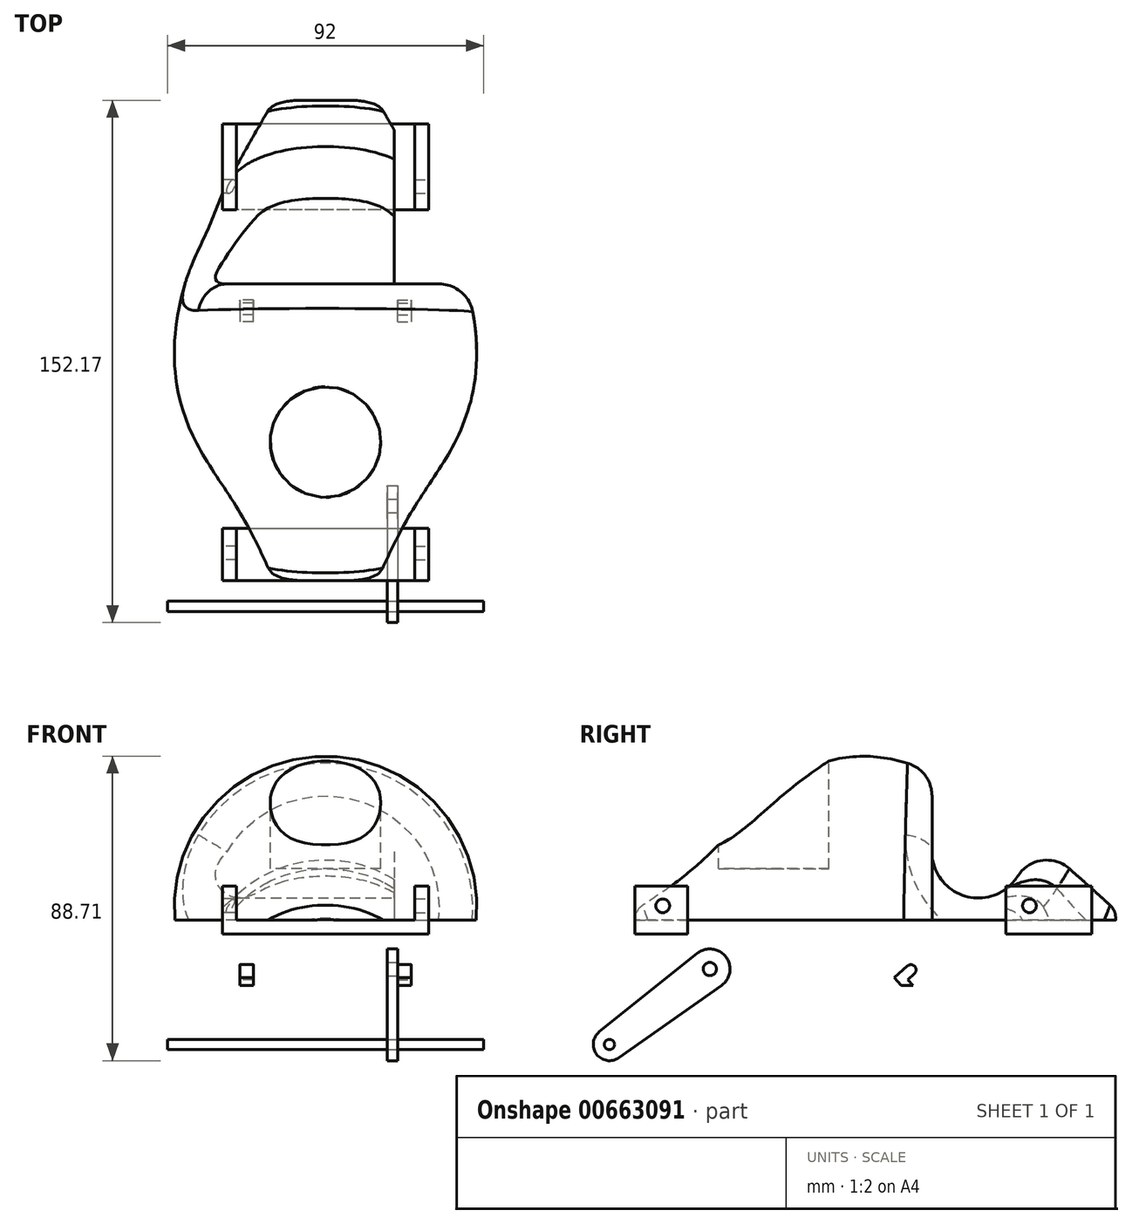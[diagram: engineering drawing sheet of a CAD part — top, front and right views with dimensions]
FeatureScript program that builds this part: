
annotation { "Feature Type Name" : "Feature", "Feature Type Description" : "" }
export const myFeature = defineFeature(function(context is Context, id is Id, definition is map)
    precondition{}
    {
        {
            var Q0;
            Q0=qCreatedBy(makeId("Front.planeOp"),FACE);
            var sketch = newSketch(context, id + "F0", { "sketchPlane" : qUnion([Q0])});
            skLineSegment(sketch, "E0.bottom", {"start": v(40, 0) * mm, "end": v(-40, 0) * mm});
            skLineSegment(sketch, "E0.top", {"start": v(40, 50) * mm, "end": v(-40, 50) * mm});
            skLineSegment(sketch, "E0.left", {"start": v(40, 0) * mm, "end": v(40, 50) * mm});
            skLineSegment(sketch, "E0.right", {"start": v(-40, 0) * mm, "end": v(-40, 50) * mm});
            skPoint(sketch, "E0.middle", {"position": v(0, 25) * mm});
            skArc(sketch, "E1", {"start": v(15, 0) * mm, "mid": v(0, 2.92) * mm, "end": v(-15, 0) * mm});
            skSolve(sketch);
        }
        {
            var Q0;
            Q0=qCreatedBy(makeId("Front.planeOp"),FACE);
            cPlane(context, id + "F1", {"entities" : qUnion([Q0]), "cplaneType" : CPlaneType.OFFSET, "offset" : 20 * mm, "oppositeDirection" : true, "width" : 150 * mm, "height" : 150 * mm});
        }
        {
            var Q0;
            Q0=qCreatedBy(id+"F1.planeOp",FACE);
            var sketch = newSketch(context, id + "F2", { "sketchPlane" : qUnion([Q0])});
            skLineSegment(sketch, "E2.0", {"start": v(40, 50) * mm, "end": v(-40, 50) * mm});
            skLineSegment(sketch, "E3.0", {"start": v(-40, 0) * mm, "end": v(-40, 50) * mm});
            skLineSegment(sketch, "E4.0", {"start": v(40, 0) * mm, "end": v(40, 50) * mm});
            skLineSegment(sketch, "E5.0", {"start": v(40, 0) * mm, "end": v(-40, 0) * mm});
            skArc(sketch, "E6", {"start": v(25, 0) * mm, "mid": v(0, 17.78) * mm, "end": v(-25, 0) * mm});
            skSolve(sketch);
        }
        {
            var Q0;
            Q0=qCreatedBy(makeId("Front.planeOp"),FACE);
            cPlane(context, id + "F3", {"entities" : qUnion([Q0]), "cplaneType" : CPlaneType.OFFSET, "offset" : 40 * mm, "oppositeDirection" : true, "width" : 150 * mm, "height" : 150 * mm});
        }
        {
            var Q0;
            Q0=qCreatedBy(id+"F3.planeOp",FACE);
            var sketch = newSketch(context, id + "F4", { "sketchPlane" : qUnion([Q0])});
            skLineSegment(sketch, "E7.0", {"start": v(40, 50) * mm, "end": v(-40, 50) * mm});
            skLineSegment(sketch, "E8.0", {"start": v(40, 0) * mm, "end": v(40, 50) * mm});
            skLineSegment(sketch, "E9.0", {"start": v(-40, 0) * mm, "end": v(-40, 50) * mm});
            skLineSegment(sketch, "E10.0", {"start": v(40, 0) * mm, "end": v(-40, 0) * mm});
            skArc(sketch, "E11", {"start": v(37.5, 0) * mm, "mid": v(0, 37.5) * mm, "end": v(-37.5, 0) * mm});
            skSolve(sketch);
        }
        {
            var Q0;
            Q0=qCreatedBy(makeId("Front.planeOp"),FACE);
            cPlane(context, id + "F5", {"entities" : qUnion([Q0]), "cplaneType" : CPlaneType.OFFSET, "offset" : 140 * mm, "oppositeDirection" : true, "width" : 150 * mm, "height" : 150 * mm});
        }
        {
            var Q0;
            Q0=qCreatedBy(id+"F5.planeOp",FACE);
            var sketch = newSketch(context, id + "F6", { "sketchPlane" : qUnion([Q0])});
            skLineSegment(sketch, "E12.0", {"start": v(40, 50) * mm, "end": v(-40, 50) * mm});
            skLineSegment(sketch, "E13.0", {"start": v(-40, 0) * mm, "end": v(-40, 50) * mm});
            skLineSegment(sketch, "E14.0", {"start": v(40, 0) * mm, "end": v(-40, 0) * mm});
            skLineSegment(sketch, "E15.0", {"start": v(40, 0) * mm, "end": v(40, 50) * mm});
            skArc(sketch, "E16.0", {"start": v(15, 0) * mm, "mid": v(0, 2.92) * mm, "end": v(-15, 0) * mm});
            skSolve(sketch);
        }
        {
            var Q0;
            {var subQ0=sQuery(id+"F0.wireOp",EDGE,"E1");Q0=makeQuery(id+"F0.imprint","IMPRINT",FACE,{"disambiguationData":[TD([[makeQuery(id+"F0.imprint","IMPRINT",EDGE,{"derivedFrom":subQ0}),1.0]])]});}
            var Q1;
            {var subQ0=sQuery(id+"F2.wireOp",EDGE,"E6");Q1=makeQuery(id+"F2.imprint","IMPRINT",FACE,{"disambiguationData":[TD([[makeQuery(id+"F2.imprint","IMPRINT",EDGE,{"derivedFrom":subQ0}),1.0]])]});}
            var Q2;
            {var subQ0=sQuery(id+"F4.wireOp",EDGE,"E11");Q2=makeQuery(id+"F4.imprint","IMPRINT",FACE,{"disambiguationData":[TD([[makeQuery(id+"F4.imprint","IMPRINT",EDGE,{"derivedFrom":subQ0}),1.0]])]});}
            var Q3;
            {var subQ0=sQuery(id+"F6.wireOp",EDGE,"E16.0");Q3=makeQuery(id+"F6.imprint","IMPRINT",FACE,{"disambiguationData":[TD([[makeQuery(id+"F6.imprint","IMPRINT",EDGE,{"derivedFrom":subQ0}),1.0]])]});}
            loft(context, id + "F7", {"sheetProfilesArray" : [{ "sheetProfileEntities" : qUnion([Q0]) }, { "sheetProfileEntities" : qUnion([Q1]) }, { "sheetProfileEntities" : qUnion([Q2]) }, { "sheetProfileEntities" : qUnion([Q3]) }]});
        }
        {
            var Q0;
            Q0=qCreatedBy(makeId("Right.planeOp"),FACE);
            var sketch = newSketch(context, id + "F8", { "sketchPlane" : qUnion([Q0])});
            skArc(sketch, "E17", {"start": v(86.5, 20) * mm, "mid": v(100, 6.5) * mm, "end": v(113.5, 20) * mm});
            skLineSegment(sketch, "E18", {"start": v(86.5, 20) * mm, "end": v(86.5, 52.12) * mm});
            skLineSegment(sketch, "E19", {"start": v(113.5, 20) * mm, "end": v(113.5, 39.76) * mm});
            skLineSegment(sketch, "E20", {"start": v(86.5, 52.12) * mm, "end": v(113.5, 39.76) * mm});
            skFitSpline(sketch, "E21.0", {"points": [v(40, 0) * mm, v(73.33, 0) * mm, v(106.67, 0) * mm, v(140, 0) * mm]});
            skLineSegment(sketch, "E22", {"start": v(86.5, 20) * mm, "end": v(113.5, 20) * mm, "construction": true});
            skSolve(sketch);
        }
        {
            var Q0;
            Q0=makeQuery(id+"F8.imprint","IMPRINT",FACE,{"disambiguationData":[TD([[makeQuery(id+"F8.imprint","IMPRINT",EDGE,{"derivedFrom":sQuery(id+"F8.wireOp",EDGE,"E17")}),1.0]])]});
            extrude(context, id + "F9", {"entities" : qUnion([Q0]), "operationType" : NewBodyOperationType.REMOVE, "endBound" : BoundingType.THROUGH_ALL, "oppositeDirection" : true, "depth" : 25 * mm, "offsetDistance" : 25 * mm, "hasSecondDirection" : true, "secondDirectionBound" : SecondDirectionBoundingType.THROUGH_ALL, "secondDirectionOppositeDirection" : false, "secondDirectionDepth" : 25 * mm});
        }
        {
            var Q0;
            Q0=qCreatedBy(makeId("Top.planeOp"),FACE);
            var sketch = newSketch(context, id + "F10", { "sketchPlane" : qUnion([Q0])});
            skLineSegment(sketch, "E23.bottom", {"start": v(20, 140) * mm, "end": v(45, 140) * mm});
            skLineSegment(sketch, "E23.top", {"start": v(20, 86.5) * mm, "end": v(45, 86.5) * mm});
            skLineSegment(sketch, "E23.left", {"start": v(20, 140) * mm, "end": v(20, 86.5) * mm});
            skLineSegment(sketch, "E23.right", {"start": v(45, 140) * mm, "end": v(45, 86.5) * mm});
            skFitSpline(sketch, "E24.0", {"points": [v(37.11, 86.5) * mm, v(12.37, 86.5) * mm, v(-12.37, 86.5) * mm, v(-37.11, 86.5) * mm], "construction": true});
            skLineSegment(sketch, "E25.0", {"start": v(-15, 140) * mm, "end": v(15, 140) * mm});
            skSolve(sketch);
        }
        {
            var Q0;
            Q0=makeQuery(id+"F10.imprint","IMPRINT",FACE,{"disambiguationData":[TD([[makeQuery(id+"F10.imprint","IMPRINT",EDGE,{"derivedFrom":sQuery(id+"F10.wireOp",EDGE,"E23.bottom")}),-1.0]])]});
            extrude(context, id + "F11", {"entities" : qUnion([Q0]), "operationType" : NewBodyOperationType.REMOVE, "endBound" : BoundingType.THROUGH_ALL, "depth" : 25 * mm, "offsetDistance" : 25 * mm});
        }
        {
            var Q0;
            {var subQ0=sQuery(id+"F2.wireOp",EDGE,"E6");var subQ1=sQuery(id+"F2.wireOp",EDGE,"E5.0");var subQ2=sQuery(id+"F0.wireOp",EDGE,"E1");var subQ3=sQuery(id+"F0.wireOp",EDGE,"E0.bottom");Q0=makeQuery(id+"F11.boolean.opBoolean","INTERSECT",EDGE,{"derivedFrom":[makeQuery(id+"F7.opLoft","SWEPT_FACE",FACE,{"disambiguationData":[OSD([subQ3,subQ2,subQ1,subQ0]),TDD([makeQuery(id+"F0.imprint","INTERSECT",VERTEX,{"disambiguationData":[OD(0.0)],"derivedFrom":[subQ3,subQ2]}),makeQuery(id+"F0.imprint","INTERSECT",VERTEX,{"disambiguationData":[OD(1.0)],"derivedFrom":[subQ3,subQ2]}),makeQuery(id+"F0.imprint","IMPRINT",EDGE,{"derivedFrom":subQ2}),makeQuery(id+"F2.imprint","INTERSECT",VERTEX,{"disambiguationData":[OD(0.0)],"derivedFrom":[subQ1,subQ0]}),makeQuery(id+"F2.imprint","INTERSECT",VERTEX,{"disambiguationData":[OD(1.0)],"derivedFrom":[subQ1,subQ0]}),makeQuery(id+"F2.imprint","IMPRINT",EDGE,{"derivedFrom":subQ0})])]}),makeQuery(id+"F11.opExtrude","SWEPT_FACE",FACE,{"disambiguationData":[OSD([sQuery(id+"F10.wireOp",EDGE,"E23.top")])]})]});}
            fillet(context, id + "F12", {"entities" : qUnion([Q0]), "radius" : 10 * mm, "tangentPropagation" : true, "allowEdgeOverflow" : false});
        }
        {
            var Q0;
            {var subQ0=sQuery(id+"F6.wireOp",EDGE,"E16.0");var subQ1=sQuery(id+"F6.wireOp",EDGE,"E14.0");Q0=makeQuery(id+"F7.opLoft","MID_CAP_EDGE",EDGE,{"disambiguationData":[OSD([subQ1,subQ0]),TDD([makeQuery(id+"F6.imprint","INTERSECT",VERTEX,{"disambiguationData":[OD(0.0)],"derivedFrom":[subQ1,subQ0]}),makeQuery(id+"F6.imprint","INTERSECT",VERTEX,{"disambiguationData":[OD(1.0)],"derivedFrom":[subQ1,subQ0]}),makeQuery(id+"F6.imprint","IMPRINT",EDGE,{"derivedFrom":subQ0})])],"capPos":3.0});}
            var Q1;
            {var subQ0=sQuery(id+"F0.wireOp",EDGE,"E1");var subQ1=sQuery(id+"F0.wireOp",EDGE,"E0.bottom");Q1=makeQuery(id+"F7.opLoft","MID_CAP_EDGE",EDGE,{"disambiguationData":[OSD([subQ1,subQ0]),TDD([makeQuery(id+"F0.imprint","INTERSECT",VERTEX,{"disambiguationData":[OD(0.0)],"derivedFrom":[subQ1,subQ0]}),makeQuery(id+"F0.imprint","INTERSECT",VERTEX,{"disambiguationData":[OD(1.0)],"derivedFrom":[subQ1,subQ0]}),makeQuery(id+"F0.imprint","IMPRINT",EDGE,{"derivedFrom":subQ0})])],"capPos":0.0});}
            fillet(context, id + "F13", {"entities" : qUnion([Q0, Q1]), "radius" : 5 * mm, "tangentPropagation" : true, "allowEdgeOverflow" : false});
        }
        {
            var Q0;
            {var subQ0=sQuery(id+"F2.wireOp",EDGE,"E6");var subQ1=sQuery(id+"F2.wireOp",EDGE,"E5.0");var subQ2=makeQuery(id+"F2.imprint","INTERSECT",VERTEX,{"disambiguationData":[OD(0.0)],"derivedFrom":[subQ1,subQ0]});var subQ3=makeQuery(id+"F2.imprint","INTERSECT",VERTEX,{"disambiguationData":[OD(1.0)],"derivedFrom":[subQ1,subQ0]});var subQ4=sQuery(id+"F0.wireOp",EDGE,"E1");var subQ5=sQuery(id+"F0.wireOp",EDGE,"E0.bottom");var subQ6=makeQuery(id+"F0.imprint","INTERSECT",VERTEX,{"disambiguationData":[OD(0.0)],"derivedFrom":[subQ5,subQ4]});var subQ7=makeQuery(id+"F0.imprint","INTERSECT",VERTEX,{"disambiguationData":[OD(1.0)],"derivedFrom":[subQ5,subQ4]});Q0=makeQuery(id+"F7.opLoft","SWEPT_FACE",FACE,{"disambiguationData":[OSD([subQ5,subQ4,subQ1,subQ0]),TDD([subQ6,subQ7,makeQuery(id+"F0.imprint","IMPRINT",EDGE,{"disambiguationData":[TD([[subQ6,-1.0]])],"derivedFrom":subQ5}),subQ2,subQ3,makeQuery(id+"F2.imprint","IMPRINT",EDGE,{"disambiguationData":[TD([[subQ2,-1.0]])],"derivedFrom":subQ1})])]});}
            var sketch = newSketch(context, id + "F14", { "sketchPlane" : qUnion([Q0])});
            skLineSegment(sketch, "E26", {"start": v(29.99, -133.07) * mm, "end": v(0, -133.07) * mm});
            skLineSegment(sketch, "E27", {"start": v(0, -133.07) * mm, "end": v(0, 0) * mm});
            skLineSegment(sketch, "E28", {"start": v(29.99, -133.07) * mm, "end": v(29.99, -108.07) * mm});
            skLineSegment(sketch, "E29", {"start": v(29.99, -108.07) * mm, "end": v(25, -108.07) * mm});
            skLineSegment(sketch, "E30", {"start": v(25, -108.07) * mm, "end": v(25, -15.29) * mm});
            skLineSegment(sketch, "E31", {"start": v(25, -15.29) * mm, "end": v(29.99, -15.29) * mm});
            skLineSegment(sketch, "E32", {"start": v(29.99, -15.29) * mm, "end": v(29.99, 0) * mm});
            skLineSegment(sketch, "E33", {"start": v(29.99, 0) * mm, "end": v(0, 0) * mm});
            skSolve(sketch);
        }
        {
            var Q0;
            {var subQ12=sQuery(id+"F14.wireOp",EDGE,"E31");Q0=makeQuery(id+"F14.imprint","IMPRINT",FACE,{"disambiguationData":[TD([[makeQuery(id+"F14.imprint","IMPRINT",EDGE,{"derivedFrom":subQ12}),1.0]])]});}
            var Q1;
            {var subQ0=sQuery(id+"F14.wireOp",EDGE,"E27");Q1=makeQuery(id+"F14.imprint","IMPRINT",FACE,{"disambiguationData":[TD([[makeQuery(id+"F14.imprint","IMPRINT",EDGE,{"derivedFrom":subQ0}),-1.0]])]});}
            var Q2;
            {var subQ1=sQuery(id+"F14.wireOp",EDGE,"E28");Q2=makeQuery(id+"F14.imprint","IMPRINT",FACE,{"disambiguationData":[TD([[makeQuery(id+"F14.imprint","IMPRINT",EDGE,{"derivedFrom":subQ1}),1.0]])]});}
            extrude(context, id + "F15", {"entities" : qUnion([Q0, Q1, Q2]), "depth" : 4 * mm, "offsetDistance" : 25 * mm});
        }
        {
            var Q0;
            {var subQ10=sQuery(id+"F14.wireOp",EDGE,"E30");var subQ11=sQuery(id+"F14.wireOp",EDGE,"E31");var subQ12=sQuery(id+"F14.wireOp",EDGE,"E32");var subQ13=sQuery(id+"F14.wireOp",EDGE,"E33");Q0=makeQuery(id+"F15.boolean.opBoolean","SPLIT",FACE,{"disambiguationData":[TD([makeQuery(id+"F15.opExtrude","SWEPT_FACE",FACE,{"disambiguationData":[OSD([subQ11])]})])],"derivedFrom":makeQuery(id+"F15.opExtrude","CAP_FACE",FACE,{"disambiguationData":[OSD([sQuery(id+"F14.wireOp",EDGE,"E26"),sQuery(id+"F14.wireOp",EDGE,"E27"),sQuery(id+"F14.wireOp",EDGE,"E28"),sQuery(id+"F14.wireOp",EDGE,"E29"),subQ10,subQ11,subQ12,subQ13])],"isStart":true})});}
            var sketch = newSketch(context, id + "F16", { "sketchPlane" : qUnion([Q0])});
            skLineSegment(sketch, "E34.0", {"start": v(29.99, 0) * mm, "end": v(0, 0) * mm});
            skPoint(sketch, "E35.0", {"position": v(29.99, 7.64) * mm});
            skLineSegment(sketch, "E36.0", {"start": v(25, 15.29) * mm, "end": v(29.99, 15.29) * mm});
            skLineSegment(sketch, "E37.0", {"start": v(29.99, 15.29) * mm, "end": v(29.99, 0) * mm});
            skLineSegment(sketch, "E38.0", {"start": v(29.99, 108.07) * mm, "end": v(25, 108.07) * mm});
            skLineSegment(sketch, "E39.0", {"start": v(29.99, 133.07) * mm, "end": v(29.99, 108.07) * mm});
            skLineSegment(sketch, "E40.0", {"start": v(29.99, 133.07) * mm, "end": v(19.02, 133.07) * mm});
            skLineSegment(sketch, "E41", {"start": v(25.99, 108.07) * mm, "end": v(25.99, 133.07) * mm});
            skLineSegment(sketch, "E42", {"start": v(25.99, 15.29) * mm, "end": v(25.99, 0) * mm});
            skSolve(sketch);
        }
        {
            var Q0;
            {var subQ0=sQuery(id+"F16.wireOp",EDGE,"E37.0");Q0=makeQuery(id+"F16.imprint","IMPRINT",FACE,{"disambiguationData":[TD([[makeQuery(id+"F16.imprint","IMPRINT",EDGE,{"derivedFrom":subQ0}),-1.0]])]});}
            var Q1;
            {var subQ0=sQuery(id+"F16.wireOp",EDGE,"E39.0");Q1=makeQuery(id+"F16.imprint","IMPRINT",FACE,{"disambiguationData":[TD([[makeQuery(id+"F16.imprint","IMPRINT",EDGE,{"derivedFrom":subQ0}),-1.0]])]});}
            extrude(context, id + "F17", {"entities" : qUnion([Q0, Q1]), "operationType" : NewBodyOperationType.ADD, "depth" : 10 * mm, "offsetDistance" : 25 * mm});
        }
        {
            var Q0;
            Q0=makeQuery(id+"F17.boolean.opBoolean","MERGE",FACE,{"derivedFrom":[makeQuery(id+"F15.opExtrude","SWEPT_FACE",FACE,{"disambiguationData":[OSD([sQuery(id+"F14.wireOp",EDGE,"E32")])]}),makeQuery(id+"F17.opExtrude","SWEPT_FACE",FACE,{"disambiguationData":[OSD([sQuery(id+"F16.wireOp",EDGE,"E37.0")])]})]});
            var sketch = newSketch(context, id + "F18", { "sketchPlane" : qUnion([Q0])});
            skCircle(sketch, "E43", {"center": v(8.07, 4.23) * mm, "radius": 2 * mm});
            skCircle(sketch, "E44", {"center": v(114.89, 4.23) * mm, "radius": 2 * mm});
            skSolve(sketch);
        }
        {
            var Q0;
            Q0=makeQuery(id+"F18.imprint","IMPRINT",FACE,{"disambiguationData":[TD([[makeQuery(id+"F18.imprint","IMPRINT",EDGE,{"derivedFrom":sQuery(id+"F18.wireOp",EDGE,"E43")}),1.0]])]});
            var Q1;
            Q1=makeQuery(id+"F18.imprint","IMPRINT",FACE,{"disambiguationData":[TD([[makeQuery(id+"F18.imprint","IMPRINT",EDGE,{"derivedFrom":sQuery(id+"F18.wireOp",EDGE,"E44")}),1.0]])]});
            extrude(context, id + "F19", {"entities" : qUnion([Q0, Q1]), "operationType" : NewBodyOperationType.REMOVE, "endBound" : BoundingType.UP_TO_NEXT, "oppositeDirection" : true, "depth" : 4 * mm, "offsetDistance" : 25 * mm});
        }
        {
            var Q0;
            Q0=makeQuery(id+"F15.opExtrude","CAP_FACE",FACE,{"disambiguationData":[OSD([sQuery(id+"F14.wireOp",EDGE,"E26"),sQuery(id+"F14.wireOp",EDGE,"E27"),sQuery(id+"F14.wireOp",EDGE,"E28"),sQuery(id+"F14.wireOp",EDGE,"E29"),sQuery(id+"F14.wireOp",EDGE,"E30"),sQuery(id+"F14.wireOp",EDGE,"E31"),sQuery(id+"F14.wireOp",EDGE,"E32"),sQuery(id+"F14.wireOp",EDGE,"E33")])],"isStart":false});
            var sketch = newSketch(context, id + "F20", { "sketchPlane" : qUnion([Q0])});
            skLineSegment(sketch, "E45.0", {"start": v(25, -108.07) * mm, "end": v(25, -15.29) * mm});
            skLineSegment(sketch, "E46", {"start": v(25, -15.29) * mm, "end": v(21, -15.29) * mm});
            skLineSegment(sketch, "E47", {"start": v(21, -15.29) * mm, "end": v(21, -108.07) * mm});
            skLineSegment(sketch, "E48", {"start": v(21, -108.07) * mm, "end": v(25, -108.07) * mm});
            skSolve(sketch);
        }
        {
            var Q0;
            Q0=makeQuery(id+"F20.imprint","IMPRINT",FACE,{"disambiguationData":[TD([[makeQuery(id+"F20.imprint","IMPRINT",EDGE,{"derivedFrom":sQuery(id+"F20.wireOp",EDGE,"E45.0")}),1.0]])]});
            extrude(context, id + "F21", {"entities" : qUnion([Q0]), "operationType" : NewBodyOperationType.ADD, "depth" : 15 * mm, "offsetDistance" : 25 * mm});
        }
        {
            var Q0;
            Q0=makeQuery(id+"F21.boolean.opBoolean","MERGE",FACE,{"derivedFrom":[makeQuery(id+"F15.opExtrude","SWEPT_FACE",FACE,{"disambiguationData":[OSD([sQuery(id+"F14.wireOp",EDGE,"E30")])]}),makeQuery(id+"F21.opExtrude","SWEPT_FACE",FACE,{"disambiguationData":[OSD([sQuery(id+"F20.wireOp",EDGE,"E45.0")])]})]});
            var sketch = newSketch(context, id + "F22", { "sketchPlane" : qUnion([Q0])});
            skCircle(sketch, "E49", {"center": v(21.79, -14.2) * mm, "radius": 1.93 * mm});
            skCircle(sketch, "E50", {"center": v(103.1, -14.2) * mm, "radius": 1.93 * mm});
            skLineSegment(sketch, "E51.0", {"start": v(108.07, -19) * mm, "end": v(15.29, -19) * mm});
            skArc(sketch, "E52", {"start": v(44, -13.31) * mm, "mid": v(41.86, -13.45) * mm, "end": v(42, -15.58) * mm});
            skLineSegment(sketch, "E53", {"start": v(61.68, -19) * mm, "end": v(61.68, -4.55) * mm, "construction": true});
            skLineSegment(sketch, "E54", {"start": v(42, -15.58) * mm, "end": v(43.93, -17.29) * mm});
            skLineSegment(sketch, "E55", {"start": v(44, -13.31) * mm, "end": v(47.87, -16.74) * mm});
            skLineSegment(sketch, "E56", {"start": v(43.93, -17.29) * mm, "end": v(42.42, -19) * mm});
            skLineSegment(sketch, "E57", {"start": v(45.87, -19) * mm, "end": v(47.87, -16.74) * mm});
            skPoint(sketch, "E58.orphan", {"position": v(50.44, -19) * mm});
            skArc(sketch, "E59.MirrorCS", {"start": v(79.36, -13.31) * mm, "mid": v(81.5, -13.45) * mm, "end": v(81.36, -15.58) * mm});
            skLineSegment(sketch, "E60.MirrorCS", {"start": v(79.36, -13.31) * mm, "end": v(75.48, -16.74) * mm});
            skLineSegment(sketch, "E61.MirrorCS", {"start": v(81.36, -15.58) * mm, "end": v(79.42, -17.29) * mm});
            skLineSegment(sketch, "E62.MirrorCS", {"start": v(79.42, -17.29) * mm, "end": v(80.93, -19) * mm});
            skLineSegment(sketch, "E63.MirrorCS", {"start": v(77.48, -19) * mm, "end": v(75.48, -16.74) * mm});
            skSolve(sketch);
        }
        {
            var Q0;
            Q0=makeQuery(id+"F22.imprint","IMPRINT",FACE,{"disambiguationData":[TD([[makeQuery(id+"F22.imprint","IMPRINT",EDGE,{"derivedFrom":sQuery(id+"F22.wireOp",EDGE,"E49")}),1.0]])]});
            var Q1;
            Q1=makeQuery(id+"F22.imprint","IMPRINT",FACE,{"disambiguationData":[TD([[makeQuery(id+"F22.imprint","IMPRINT",EDGE,{"derivedFrom":sQuery(id+"F22.wireOp",EDGE,"E50")}),1.0]])]});
            var Q2;
            Q2=makeQuery(id+"F22.imprint","IMPRINT",FACE,{"disambiguationData":[TD([[makeQuery(id+"F22.imprint","IMPRINT",EDGE,{"derivedFrom":sQuery(id+"F22.wireOp",EDGE,"E52")}),1.0]])]});
            var Q3;
            {var subQ0=sQuery(id+"F22.wireOp",EDGE,"4ae6c853-88ae-48ed-967d-8e219ce0fb7c0.MirrorCS");Q3=makeQuery(id+"F22.imprint","IMPRINT",FACE,{"disambiguationData":[TD([[makeQuery(id+"F22.imprint","IMPRINT",EDGE,{"derivedFrom":subQ0}),-1.0]])]});}
            var Q4;
            Q4=makeQuery(id+"F22.imprint","IMPRINT",FACE,{"disambiguationData":[TD([[makeQuery(id+"F22.imprint","IMPRINT",EDGE,{"derivedFrom":sQuery(id+"F22.wireOp",EDGE,"E59.MirrorCS")}),-1.0]])]});
            extrude(context, id + "F23", {"entities" : qUnion([Q0, Q1, Q2, Q3, Q4]), "operationType" : NewBodyOperationType.REMOVE, "endBound" : BoundingType.UP_TO_NEXT, "oppositeDirection" : true, "depth" : 25 * mm, "offsetDistance" : 25 * mm});
        }
        {
            var Q0;
            Q0=makeQuery(id+"F15.opExtrude","SWEPT_BODY",BODY,{"disambiguationData":[OSD([sQuery(id+"F14.wireOp",EDGE,"E26"),sQuery(id+"F14.wireOp",EDGE,"E27"),sQuery(id+"F14.wireOp",EDGE,"E28"),sQuery(id+"F14.wireOp",EDGE,"E29"),sQuery(id+"F14.wireOp",EDGE,"E30"),sQuery(id+"F14.wireOp",EDGE,"E31"),sQuery(id+"F14.wireOp",EDGE,"E32"),sQuery(id+"F14.wireOp",EDGE,"E33")])]});
            var Q1;
            Q1=makeQuery(id+"F15.opExtrude","SWEPT_FACE",FACE,{"disambiguationData":[OSD([sQuery(id+"F14.wireOp",EDGE,"E27")])]});
            mirror(context, id + "F24", {"operationType" : NewBodyOperationType.ADD, "entities" : qUnion([Q0]), "mirrorPlane" : qUnion([Q1])});
        }
        {
            var Q0;
            Q0=makeQuery(id+"F21.opExtrude","SWEPT_FACE",FACE,{"disambiguationData":[OSD([sQuery(id+"F20.wireOp",EDGE,"E47")])]});
            var sketch = newSketch(context, id + "F25", { "sketchPlane" : qUnion([Q0])});
            skCircle(sketch, "E64.0", {"center": v(-21.79, -14.2) * mm, "radius": 1.93 * mm});
            skArc(sketch, "E65", {"start": v(-18.12, -9.63) * mm, "mid": v(-26.47, -10.68) * mm, "end": v(-25.16, -19) * mm});
            skLineSegment(sketch, "E66", {"start": v(-18.12, -9.63) * mm, "end": v(10.4, -32.5) * mm});
            skLineSegment(sketch, "E67", {"start": v(-25.16, -19) * mm, "end": v(4.73, -40.05) * mm});
            skArc(sketch, "E68", {"start": v(4.73, -40.05) * mm, "mid": v(11.22, -39.03) * mm, "end": v(10.4, -32.5) * mm});
            skCircle(sketch, "E69", {"center": v(7.45, -36.19) * mm, "radius": 1.5 * mm});
            skSolve(sketch);
        }
        {
            var Q0;
            {var subQ1=sQuery(id+"F25.wireOp",EDGE,"E67");Q0=makeQuery(id+"F25.imprint","IMPRINT",FACE,{"disambiguationData":[TD([[makeQuery(id+"F25.imprint","IMPRINT",EDGE,{"derivedFrom":subQ1}),1.0]])]});}
            var Q1;
            Q1=makeQuery(id+"F25.imprint","IMPRINT",FACE,{"disambiguationData":[TD([[makeQuery(id+"F25.imprint","IMPRINT",EDGE,{"derivedFrom":sQuery(id+"F25.wireOp",EDGE,"E64.0")}),-1.0]])]});
            extrude(context, id + "F26", {"entities" : qUnion([Q0, Q1]), "depth" : 3 * mm, "offsetDistance" : 25 * mm});
        }
        {
            var Q0;
            Q0=makeQuery(id+"F26.opExtrude","CAP_FACE",FACE,{"disambiguationData":[OSD([sQuery(id+"F25.wireOp",EDGE,"E64.0"),sQuery(id+"F25.wireOp",EDGE,"E65"),sQuery(id+"F25.wireOp",EDGE,"E66"),sQuery(id+"F25.wireOp",EDGE,"E67"),sQuery(id+"F25.wireOp",EDGE,"E68"),sQuery(id+"F25.wireOp",EDGE,"E69")])],"isStart":true});
            var sketch = newSketch(context, id + "F27", { "sketchPlane" : qUnion([Q0])});
            skCircle(sketch, "E70.0", {"center": v(-7.45, -36.19) * mm, "radius": 1.5 * mm});
            skSolve(sketch);
        }
        {
            var Q0;
            Q0=makeQuery(id+"F27.imprint","IMPRINT",FACE,{"disambiguationData":[TD([[makeQuery(id+"F27.imprint","IMPRINT",EDGE,{"derivedFrom":sQuery(id+"F27.wireOp",EDGE,"E70.0")}),-1.0]])]});
            extrude(context, id + "F28", {"entities" : qUnion([Q0]), "depth" : 25 * mm, "offsetDistance" : 25 * mm, "hasSecondDirection" : true, "secondDirectionOppositeDirection" : true, "secondDirectionDepth" : 67 * mm});
        }
        {
            var Q0;
            Q0=qCreatedBy(makeId("Top.planeOp"),FACE);
            cPlane(context, id + "F29", {"entities" : qUnion([Q0]), "cplaneType" : CPlaneType.OFFSET, "offset" : 62 * mm, "width" : 150 * mm, "height" : 150 * mm});
        }
        {
            var Q0;
            Q0=qCreatedBy(id+"F29.planeOp",FACE);
            var sketch = newSketch(context, id + "F30", { "sketchPlane" : qUnion([Q0])});
            skCircle(sketch, "E71", {"center": v(0, 40.4) * mm, "radius": 16.1 * mm});
            skSolve(sketch);
        }
        {
            var Q0;
            Q0=makeQuery(id+"F30.imprint","IMPRINT",FACE,{"disambiguationData":[TD([[makeQuery(id+"F30.imprint","IMPRINT",EDGE,{"derivedFrom":sQuery(id+"F30.wireOp",EDGE,"E71")}),1.0]])]});
            extrude(context, id + "F31", {"entities" : qUnion([Q0]), "operationType" : NewBodyOperationType.REMOVE, "oppositeDirection" : true, "depth" : 46.9 * mm, "offsetDistance" : 25 * mm});
        }
    });
